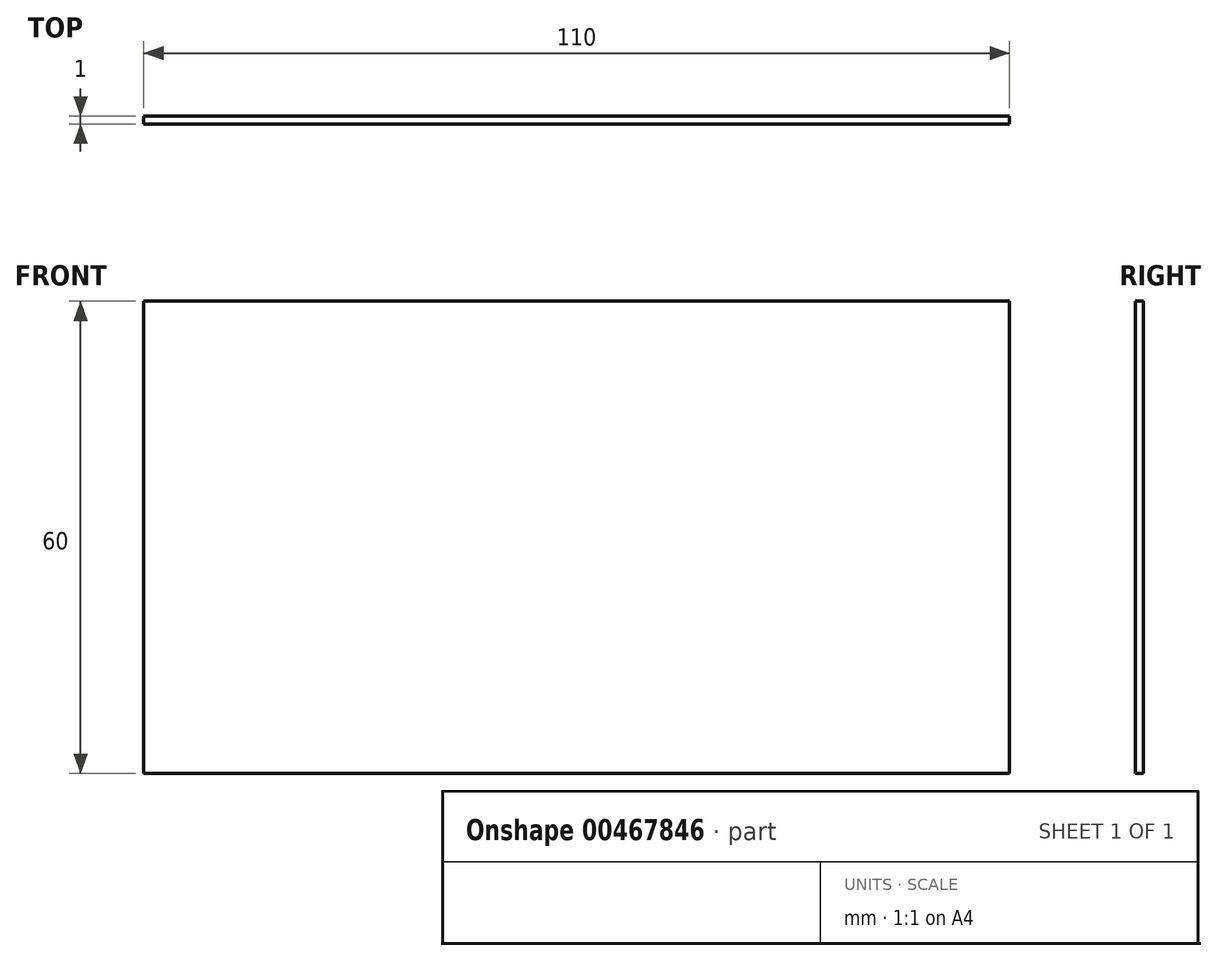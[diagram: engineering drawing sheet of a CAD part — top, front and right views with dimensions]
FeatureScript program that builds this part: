
annotation { "Feature Type Name" : "Feature", "Feature Type Description" : "" }
export const myFeature = defineFeature(function(context is Context, id is Id, definition is map)
    precondition{}
    {
        {
            var Q0;
            Q0=qCreatedBy(makeId("Top.planeOp"),FACE);
            var sketch = newSketch(context, id + "F0", { "sketchPlane" : qUnion([Q0])});
            skLineSegment(sketch, "E0.bottom", {"start": v(55, -0.5) * mm, "end": v(-55, -0.5) * mm});
            skLineSegment(sketch, "E0.top", {"start": v(55, 0.5) * mm, "end": v(-55, 0.5) * mm});
            skLineSegment(sketch, "E0.left", {"start": v(55, -0.5) * mm, "end": v(55, 0.5) * mm});
            skLineSegment(sketch, "E0.right", {"start": v(-55, -0.5) * mm, "end": v(-55, 0.5) * mm});
            skSolve(sketch);
        }
        {
            var Q0;
            Q0=makeQuery(id+"F0.imprint","IMPRINT",FACE,{"disambiguationData":[TD([[makeQuery(id+"F0.imprint","IMPRINT",EDGE,{"derivedFrom":sQuery(id+"F0.wireOp",EDGE,"E0.bottom")}),-1.0]])]});
            extrude(context, id + "F1", {"entities" : qUnion([Q0]), "depth" : 60 * mm});
        }
    });
